FCSTD DOCUMENT  (FreeCAD 0.21RUnknown)
Label: part46-sketcherReferenceConstraints
License: All rights reserved
LicenseURL: http://en.wikipedia.org/wiki/All_rights_reserved
objects: Sketcher::SketchObject×3
note: 3 computed .brp shape members not serialized (recipe doc carries the construction recipe); baked Part::Feature solids carry a one-line shape summary decoded from their .brp

FEATURE [Sketcher::SketchObject] Sketch
  FullyConstrained = true
  sketch-geometry (10):
    g0: LineSegment StartX=-50 StartY=50 StartZ=0 EndX=50 EndY=50 EndZ=0
    g1: LineSegment StartX=50 StartY=50 StartZ=0 EndX=50 EndY=-50 EndZ=0
    g2: LineSegment StartX=50 StartY=-50 StartZ=0 EndX=-50 EndY=-50 EndZ=0
    g3: LineSegment StartX=-50 StartY=-50 StartZ=0 EndX=-50 EndY=50 EndZ=0
    g4: LineSegment StartX=-40 StartY=40 StartZ=0 EndX=-15 EndY=40 EndZ=0
    g5: LineSegment StartX=-15 StartY=40 StartZ=0 EndX=-15 EndY=-35 EndZ=0
    g6: LineSegment StartX=-15 StartY=-35 StartZ=0 EndX=-40 EndY=-35 EndZ=0
    g7: LineSegment StartX=-40 StartY=-35 StartZ=0 EndX=-40 EndY=40 EndZ=0
    g8: Circle CenterX=15 CenterY=0 CenterZ=0 NormalX=0 NormalY=0 NormalZ=1 AngleXU=0 Radius=25
    g9: GeomPoint X=40 Y=0 Z=0
  constraints (29):
    c: Coincident(g0,g1)
    c: Coincident(g1,g2)
    c: Coincident(g2,g3)
    c: Coincident(g3,g0)
    c: Horizontal(g0)
    c: Horizontal(g2)
    c: Vertical(g1)
    c: Vertical(g3)
    c: Equal(g0,g3)
    c: Symmetric(g0,g1,g-1)
    c: DistanceX(g0,g0) = 100
    c: Coincident(g4,g5)
    c: Coincident(g5,g6)
    c: Coincident(g6,g7)
    c: Coincident(g7,g4)
    c: Horizontal(g4)
    c: Horizontal(g6)
    c: Vertical(g5)
    c: Vertical(g7)
    c: DistanceX(g0,g4) = 10
    c: DistanceY(g4,g0) = 10
    c: DistanceX(g6,g6) = 25
    c: DistanceY(g7,g7) = 75
    c: PointOnObject(g8,g-1)
    c: Distance(g8,g5) = 5
    c: Diameter(g8) = 50
    c: PointOnObject(g9,g8)
    c: Horizontal(g9,g8)
    c: DistanceX(g9,g0) = 10
FEATURE [Sketcher::SketchObject] Sketch001
  FullyConstrained = false
  sketch-geometry (6):
    g0: LineSegment StartX=-33.6732 StartY=33.6749 StartZ=0 EndX=20.6284 EndY=33.6749 EndZ=0
    g1: LineSegment StartX=20.6284 StartY=33.6749 StartZ=0 EndX=20.6284 EndY=-22.7459 EndZ=0
    g2: LineSegment StartX=20.6284 StartY=-22.7459 StartZ=0 EndX=-33.6732 EndY=-22.7459 EndZ=0
    g3: LineSegment StartX=-33.6732 StartY=-22.7459 StartZ=0 EndX=-33.6732 EndY=33.6749 EndZ=0
    g4: Circle CenterX=-18.3294 CenterY=18.331 CenterZ=0 NormalX=0 NormalY=0 NormalZ=1 AngleXU=0 Radius=2.5
    g5: Circle CenterX=-18.3294 CenterY=18.331 CenterZ=0 NormalX=0 NormalY=0 NormalZ=1 AngleXU=0 Radius=15.3438
  constraints (15):
    c: Coincident(g0,g1)
    c: Coincident(g1,g2)
    c: Coincident(g2,g3)
    c: Coincident(g3,g0)
    c: Horizontal(g0)
    c: Horizontal(g2)
    c: Vertical(g1)
    c: Vertical(g3)
    c: Coincident(g5,g4)
    c: Tangent(g5,g0)
    c: Tangent(g5,g3)
    c: Diameter(g4) = 5
    c: Distance(g4,g0) = 21.6994
    c: DistanceY(g4,g0) = 15.3438
    c: DistanceX(g0,g4) = 15.3438
FEATURE [Sketcher::SketchObject] Sketch002
  FullyConstrained = false
  expr: Constraints[4] = .Constraints.LeftSide * 0.75
  sketch-geometry (3):
    g0: LineSegment StartX=-22.6658 StartY=50.6126 StartZ=0 EndX=-22.6658 EndY=7.61262 EndZ=0
    g1: LineSegment StartX=-22.6658 StartY=7.61262 StartZ=0 EndX=9.58423 EndY=7.61262 EndZ=0
    g2: LineSegment StartX=-22.6658 StartY=50.6126 StartZ=0 EndX=9.58423 EndY=7.61262 EndZ=0
  constraints (8):
    c: Coincident(g0,g1)
    c: Horizontal(g1)
    c: Vertical(g0)
    c: DistanceY(g0,g0) = 43  'LeftSide'
    c: DistanceX(g1,g1) = 32.25
    c: Coincident(g2,g0)
    c: Coincident(g2,g1)
    c: Distance(g2) = 53.75
